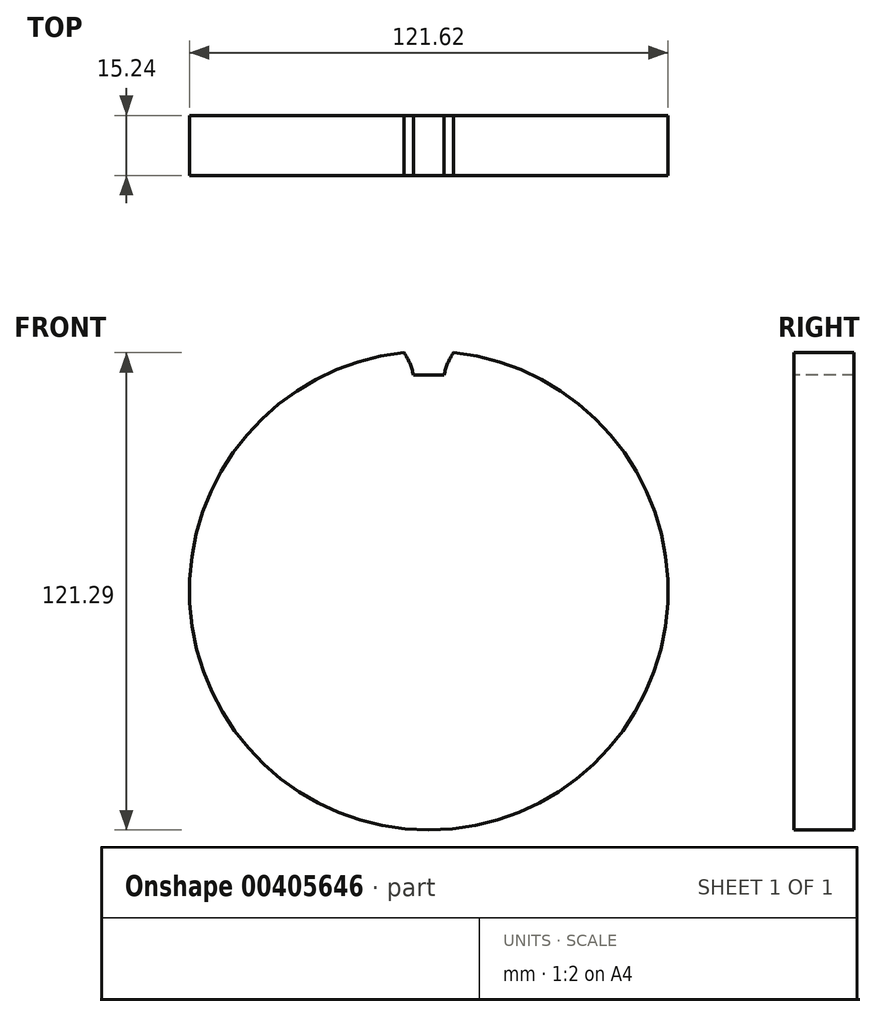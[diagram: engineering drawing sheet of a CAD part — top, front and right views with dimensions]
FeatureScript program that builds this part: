
annotation { "Feature Type Name" : "Feature", "Feature Type Description" : "" }
export const myFeature = defineFeature(function(context is Context, id is Id, definition is map)
    precondition{}
    {
        {
            var Q0;
            Q0=qCreatedBy(makeId("Front.planeOp"),FACE);
            var sketch = newSketch(context, id + "F0", { "sketchPlane" : qUnion([Q0])});
            skCircle(sketch, "E0", {"center": v(0, 0) * mm, "radius": 60.8 * mm});
            skSolve(sketch);
        }
        {
            var Q0;
            Q0 = qSketchRegion(id + "F0", true);
            extrude(context, id + "F1", {"entities" : qUnion([Q0]), "depth" : 15.24 * mm});
        }
        {
            var Q0;
            Q0=makeQuery(id+"F1.opExtrude","CAP_FACE",FACE,{"disambiguationData":[OSD([sQuery(id+"F0.wireOp",EDGE,"E0")])],"isStart":false});
            var sketch = newSketch(context, id + "F2", { "sketchPlane" : qUnion([Q0])});
            skLineSegment(sketch, "E1", {"start": v(0, 0) * mm, "end": v(0, 69.91) * mm, "construction": true});
            skArc(sketch, "E2", {"start": v(-3.9, 54.8) * mm, "mid": v(-6.06, 60.12) * mm, "end": v(-10.07, 64.22) * mm});
            skLineSegment(sketch, "E3", {"start": v(-3.9, 54.8) * mm, "end": v(0, 54.8) * mm});
            skArc(sketch, "E4.MirrorCS", {"start": v(3.9, 54.8) * mm, "mid": v(6.06, 60.12) * mm, "end": v(10.07, 64.22) * mm});
            skLineSegment(sketch, "E5.MirrorCS", {"start": v(3.9, 54.8) * mm, "end": v(0, 54.8) * mm});
            skLineSegment(sketch, "E6", {"start": v(-10.07, 64.22) * mm, "end": v(10.07, 64.22) * mm});
            skSolve(sketch);
        }
        {
            var Q0;
            {var subQ0=sQuery(id+"F2.wireOp",EDGE,"E6");Q0=makeQuery(id+"F2.imprint","IMPRINT",FACE,{"disambiguationData":[TD([[makeQuery(id+"F2.imprint","IMPRINT",EDGE,{"derivedFrom":subQ0}),-1.0]])]});}
            var Q1;
            {var subQ4=sQuery(id+"F2.wireOp",EDGE,"E3");Q1=makeQuery(id+"F2.imprint","IMPRINT",FACE,{"disambiguationData":[TD([[makeQuery(id+"F2.imprint","IMPRINT",EDGE,{"derivedFrom":subQ4}),1.0]])]});}
            extrude(context, id + "F3", {"entities" : qUnion([Q0, Q1]), "operationType" : NewBodyOperationType.REMOVE, "endBound" : BoundingType.THROUGH_ALL, "oppositeDirection" : true, "depth" : 25.4 * mm});
        }
    });
